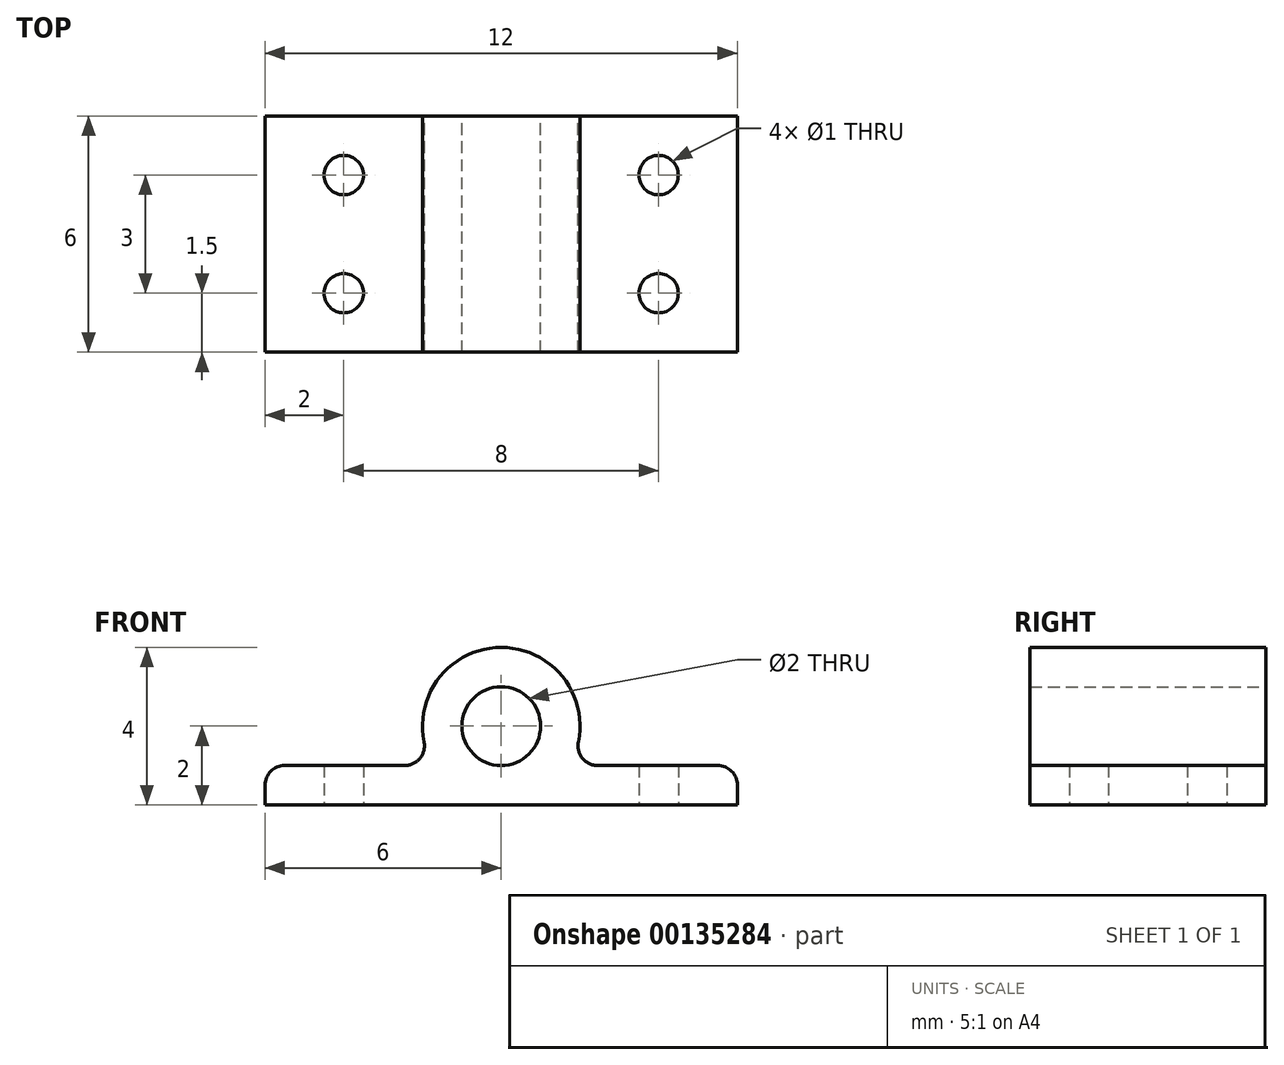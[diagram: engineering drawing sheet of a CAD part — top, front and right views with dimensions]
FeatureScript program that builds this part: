
annotation { "Feature Type Name" : "Feature", "Feature Type Description" : "" }
export const myFeature = defineFeature(function(context is Context, id is Id, definition is map)
    precondition{}
    {
        {
            var Q0;
            Q0=qCreatedBy(makeId("Front.planeOp"),FACE);
            var sketch = newSketch(context, id + "F0", { "sketchPlane" : qUnion([Q0])});
            skLineSegment(sketch, "E0.bottom", {"start": v(0, 0) * mm, "end": v(12, 0) * mm});
            skLineSegment(sketch, "E0.top", {"start": v(0, 1) * mm, "end": v(4.27, 1) * mm});
            skLineSegment(sketch, "E0.left", {"start": v(0, 0) * mm, "end": v(0, 1) * mm});
            skLineSegment(sketch, "E0.right", {"start": v(12, 0) * mm, "end": v(12, 1) * mm});
            skPoint(sketch, "E1.endSnap0", {"position": v(6, 1) * mm});
            skArc(sketch, "E2", {"start": v(7.73, 1) * mm, "mid": v(6, 4) * mm, "end": v(4.27, 1) * mm});
            skCircle(sketch, "E3", {"center": v(6, 2) * mm, "radius": 1 * mm});
            skPoint(sketch, "E4.orphan", {"position": v(6, 0) * mm});
            skLineSegment(sketch, "E5.trimOffspring", {"start": v(7.73, 1) * mm, "end": v(12, 1) * mm});
            skPoint(sketch, "E6.visualSharp", {"position": v(0, 1) * mm});
            skSolve(sketch);
        }
        {
            var Q0;
            Q0 = qSketchRegion(id + "F0", true);
            extrude(context, id + "F1", {"entities" : qUnion([Q0]), "depth" : 6 * mm});
        }
        {
            var Q0;
            Q0=makeQuery(id+"F1.opExtrude","SWEPT_FACE",FACE,{"disambiguationData":[OSD([sQuery(id+"F0.wireOp",EDGE,"E0.bottom")])]});
            var sketch = newSketch(context, id + "F2", { "sketchPlane" : qUnion([Q0])});
            skCircle(sketch, "E7", {"center": v(10, 1.5) * mm, "radius": 0.5 * mm});
            skCircle(sketch, "E8", {"center": v(10, 4.5) * mm, "radius": 0.5 * mm});
            skCircle(sketch, "E9", {"center": v(2, 4.5) * mm, "radius": 0.5 * mm});
            skCircle(sketch, "E10", {"center": v(2, 1.5) * mm, "radius": 0.5 * mm});
            skSolve(sketch);
        }
        {
            var Q0;
            Q0 = qSketchRegion(id + "F2", true);
            extrude(context, id + "F3", {"entities" : qUnion([Q0]), "operationType" : NewBodyOperationType.REMOVE, "endBound" : BoundingType.THROUGH_ALL, "oppositeDirection" : true, "depth" : 25 * mm});
        }
        {
            var Q0;
            Q0=makeQuery(id+"F1.opExtrude","SWEPT_EDGE",EDGE,{"disambiguationData":[OSD([sQuery(id+"F0.wireOp",EDGE,"E0.top"),sQuery(id+"F0.wireOp",EDGE,"E0.left")])]});
            var Q1;
            Q1=makeQuery(id+"F1.opExtrude","SWEPT_EDGE",EDGE,{"disambiguationData":[OSD([sQuery(id+"F0.wireOp",EDGE,"E0.right"),sQuery(id+"F0.wireOp",EDGE,"E5.trimOffspring")])]});
            var Q2;
            Q2=makeQuery(id+"F1.opExtrude","SWEPT_EDGE",EDGE,{"disambiguationData":[OSD([sQuery(id+"F0.wireOp",EDGE,"E2"),sQuery(id+"F0.wireOp",EDGE,"E5.trimOffspring")])]});
            var Q3;
            Q3=makeQuery(id+"F1.opExtrude","SWEPT_EDGE",EDGE,{"disambiguationData":[OSD([sQuery(id+"F0.wireOp",EDGE,"E0.top"),sQuery(id+"F0.wireOp",EDGE,"E2")])]});
            fillet(context, id + "F4", {"entities" : qUnion([Q0, Q1, Q2, Q3]), "radius" : 0.5 * mm, "tangentPropagation" : true, "allowEdgeOverflow" : false});
        }
    });
